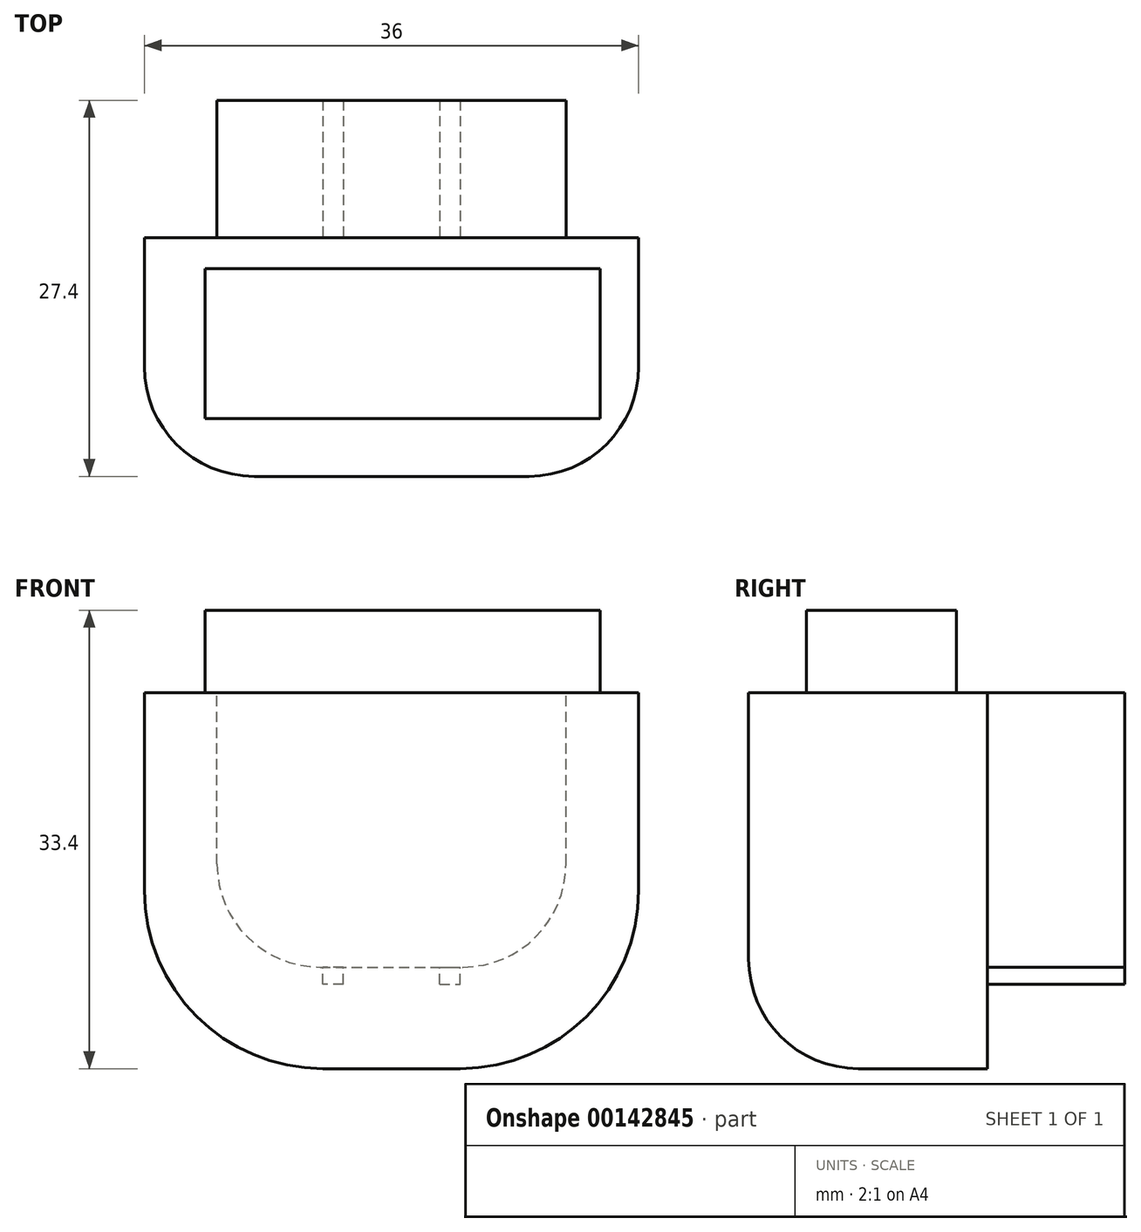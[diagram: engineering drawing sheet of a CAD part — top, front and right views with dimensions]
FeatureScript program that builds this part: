
annotation { "Feature Type Name" : "Feature", "Feature Type Description" : "" }
export const myFeature = defineFeature(function(context is Context, id is Id, definition is map)
    precondition{}
    {
        {
            var Q0;
            Q0=qCreatedBy(makeId("Top.planeOp"),FACE);
            var sketch = newSketch(context, id + "F0", { "sketchPlane" : qUnion([Q0])});
            skLineSegment(sketch, "E0.bottom", {"start": v(-18, 0) * mm, "end": v(18, 0) * mm});
            skLineSegment(sketch, "E0.top", {"start": v(-18, 17.4) * mm, "end": v(18, 17.4) * mm});
            skLineSegment(sketch, "E0.left", {"start": v(-18, 0) * mm, "end": v(-18, 17.4) * mm});
            skLineSegment(sketch, "E0.right", {"start": v(18, 0) * mm, "end": v(18, 17.4) * mm});
            skSolve(sketch);
        }
        {
            var Q0;
            Q0 = qSketchRegion(id + "F0", true);
            extrude(context, id + "F1", {"entities" : qUnion([Q0]), "depth" : 27.4 * mm});
        }
        {
            var Q0;
            Q0=makeQuery(id+"F1.opExtrude","CAP_FACE",FACE,{"disambiguationData":[OSD([sQuery(id+"F0.wireOp",EDGE,"E0.bottom"),sQuery(id+"F0.wireOp",EDGE,"E0.top"),sQuery(id+"F0.wireOp",EDGE,"E0.left"),sQuery(id+"F0.wireOp",EDGE,"E0.right")])],"isStart":false});
            var sketch = newSketch(context, id + "F2", { "sketchPlane" : qUnion([Q0])});
            skLineSegment(sketch, "E1.bottom", {"start": v(-12.7, 27.4) * mm, "end": v(12.7, 27.4) * mm});
            skLineSegment(sketch, "E1.top", {"start": v(-12.7, 17.4) * mm, "end": v(12.7, 17.4) * mm});
            skLineSegment(sketch, "E1.left", {"start": v(-12.7, 27.4) * mm, "end": v(-12.7, 17.4) * mm});
            skLineSegment(sketch, "E1.right", {"start": v(12.7, 27.4) * mm, "end": v(12.7, 17.4) * mm});
            skSolve(sketch);
        }
        {
            var Q0;
            Q0 = qSketchRegion(id + "F2", true);
            extrude(context, id + "F3", {"entities" : qUnion([Q0]), "oppositeDirection" : true, "depth" : 20 * mm});
        }
        {
            var Q0;
            Q0=makeQuery(id+"F3.opExtrude","CAP_EDGE",EDGE,{"disambiguationData":[OSD([sQuery(id+"F2.wireOp",EDGE,"E1.left")])],"isStart":false});
            var Q1;
            Q1=makeQuery(id+"F3.opExtrude","CAP_EDGE",EDGE,{"disambiguationData":[OSD([sQuery(id+"F2.wireOp",EDGE,"E1.right")])],"isStart":false});
            fillet(context, id + "F4", {"entities" : qUnion([Q0, Q1]), "radius" : 7.5 * mm, "tangentPropagation" : true, "allowEdgeOverflow" : false});
        }
        {
            var Q0;
            Q0=makeQuery(id+"F1.opExtrude","CAP_EDGE",EDGE,{"disambiguationData":[OSD([sQuery(id+"F0.wireOp",EDGE,"E0.right")])],"isStart":true});
            var Q1;
            Q1=makeQuery(id+"F1.opExtrude","CAP_EDGE",EDGE,{"disambiguationData":[OSD([sQuery(id+"F0.wireOp",EDGE,"E0.left")])],"isStart":true});
            fillet(context, id + "F5", {"entities" : qUnion([Q0, Q1]), "radius" : 13 * mm, "tangentPropagation" : true, "allowEdgeOverflow" : false});
        }
        {
            var Q0;
            Q0=makeQuery(id+"F1.opExtrude","CAP_FACE",FACE,{"disambiguationData":[OSD([sQuery(id+"F0.wireOp",EDGE,"E0.bottom"),sQuery(id+"F0.wireOp",EDGE,"E0.top"),sQuery(id+"F0.wireOp",EDGE,"E0.left"),sQuery(id+"F0.wireOp",EDGE,"E0.right")])],"isStart":false});
            var sketch = newSketch(context, id + "F6", { "sketchPlane" : qUnion([Q0])});
            skLineSegment(sketch, "E2.bottom", {"start": v(-13.58, 15.12) * mm, "end": v(15.2, 15.12) * mm});
            skLineSegment(sketch, "E2.top", {"start": v(-13.58, 4.2) * mm, "end": v(15.2, 4.2) * mm});
            skLineSegment(sketch, "E2.left", {"start": v(-13.58, 15.12) * mm, "end": v(-13.58, 4.2) * mm});
            skLineSegment(sketch, "E2.right", {"start": v(15.2, 15.12) * mm, "end": v(15.2, 4.2) * mm});
            skSolve(sketch);
        }
        {
            var Q0;
            Q0=makeQuery(id+"F6.imprint","IMPRINT",FACE,{"disambiguationData":[TD([[makeQuery(id+"F6.imprint","IMPRINT",EDGE,{"derivedFrom":sQuery(id+"F6.wireOp",EDGE,"E2.bottom")}),-1.0]])]});
            extrude(context, id + "F7", {"entities" : qUnion([Q0]), "operationType" : NewBodyOperationType.ADD, "depth" : 6 * mm});
        }
        {
            var Q0;
            Q0=makeQuery(id+"F1.opExtrude","SWEPT_EDGE",EDGE,{"disambiguationData":[OSD([sQuery(id+"F0.wireOp",EDGE,"E0.bottom"),sQuery(id+"F0.wireOp",EDGE,"E0.left")])]});
            var Q1;
            Q1=makeQuery(id+"F5.opFillet","BLEND_EDGE",EDGE,{"blendedFrom":[makeQuery(id+"F1.opExtrude","CAP_EDGE",EDGE,{"disambiguationData":[OSD([sQuery(id+"F0.wireOp",EDGE,"E0.left")])],"isStart":true}),makeQuery(id+"F1.opExtrude","SWEPT_FACE",FACE,{"disambiguationData":[OSD([sQuery(id+"F0.wireOp",EDGE,"E0.bottom")])]})],"blendedInto":[makeQuery(id+"F1.opExtrude","SWEPT_FACE",FACE,{"disambiguationData":[OSD([sQuery(id+"F0.wireOp",EDGE,"E0.bottom")])]})]});
            fillet(context, id + "F8", {"entities" : qUnion([Q0, Q1]), "radius" : 8 * mm, "tangentPropagation" : true, "allowEdgeOverflow" : false});
        }
        {
            var Q0;
            Q0=makeQuery(id+"F3.opExtrude","CAP_FACE",FACE,{"disambiguationData":[OSD([sQuery(id+"F2.wireOp",EDGE,"E1.bottom"),sQuery(id+"F2.wireOp",EDGE,"E1.top"),sQuery(id+"F2.wireOp",EDGE,"E1.left"),sQuery(id+"F2.wireOp",EDGE,"E1.right")])],"isStart":false});
            var sketch = newSketch(context, id + "F9", { "sketchPlane" : qUnion([Q0])});
            skLineSegment(sketch, "E3.bottom", {"start": v(5, -27.4) * mm, "end": v(3.5, -27.4) * mm});
            skLineSegment(sketch, "E3.top", {"start": v(5, -17.4) * mm, "end": v(3.5, -17.4) * mm});
            skLineSegment(sketch, "E3.left", {"start": v(5, -27.4) * mm, "end": v(5, -17.4) * mm});
            skLineSegment(sketch, "E3.right", {"start": v(3.5, -27.4) * mm, "end": v(3.5, -17.4) * mm});
            skSolve(sketch);
        }
        {
            var Q0;
            Q0 = qSketchRegion(id + "F9", true);
            extrude(context, id + "F10", {"entities" : qUnion([Q0]), "depth" : 1.25 * mm});
        }
        {
            var Q0;
            Q0=makeQuery(id+"F10.opExtrude","SWEPT_BODY",BODY,{"disambiguationData":[OSD([sQuery(id+"F9.wireOp",EDGE,"E3.bottom"),sQuery(id+"F9.wireOp",EDGE,"E3.top"),sQuery(id+"F9.wireOp",EDGE,"E3.left"),sQuery(id+"F9.wireOp",EDGE,"E3.right")])]});
            var Q1;
            Q1=qCreatedBy(makeId("Right.planeOp"),FACE);
            mirror(context, id + "F11", {"entities" : qUnion([Q0]), "mirrorPlane" : qUnion([Q1])});
        }
    });
